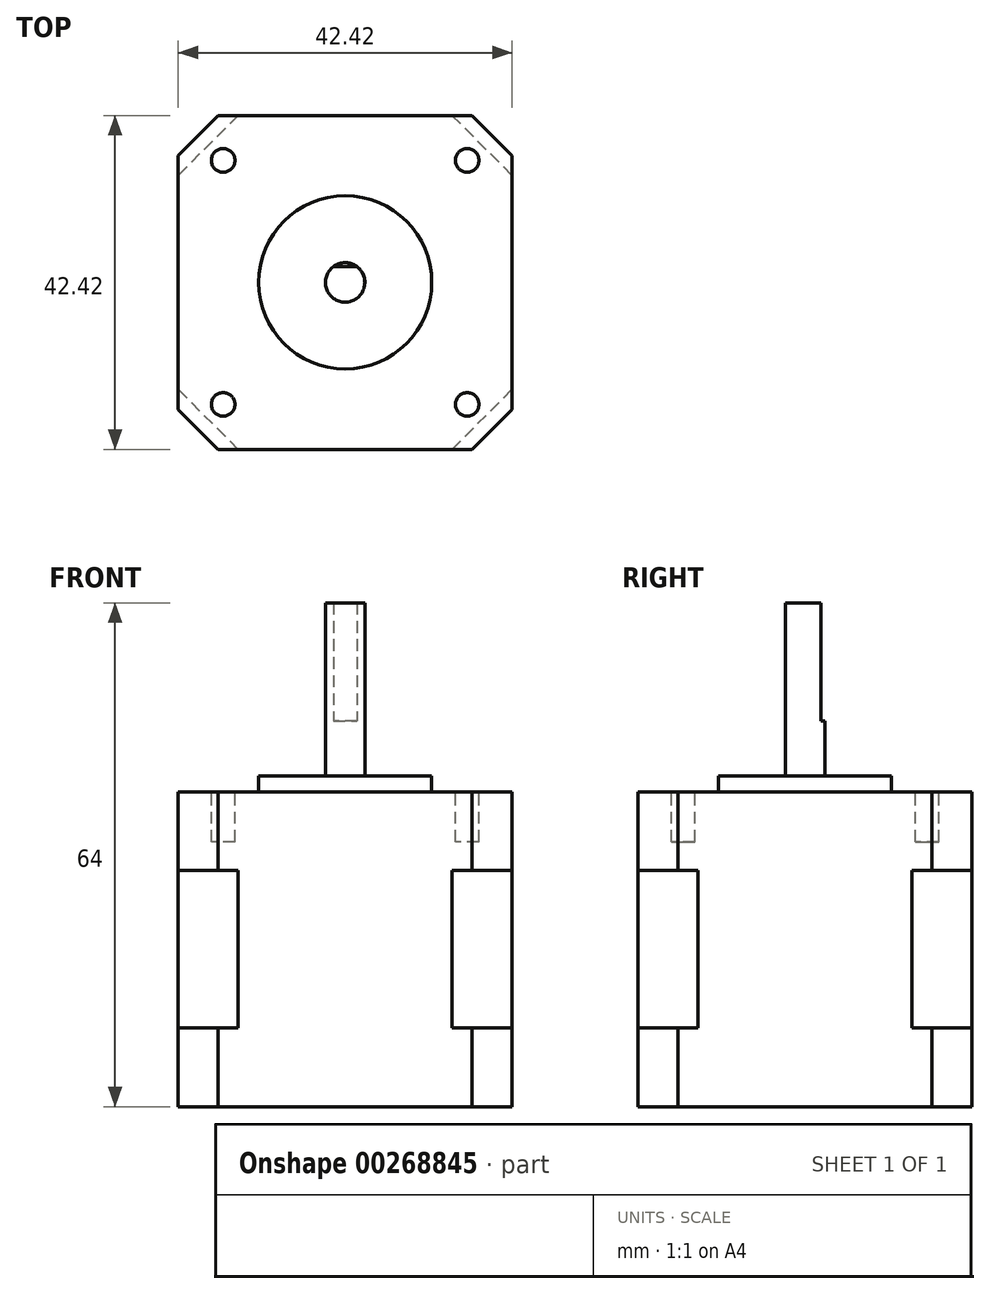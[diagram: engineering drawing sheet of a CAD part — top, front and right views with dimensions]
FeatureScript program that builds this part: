
annotation { "Feature Type Name" : "Feature", "Feature Type Description" : "" }
export const myFeature = defineFeature(function(context is Context, id is Id, definition is map)
    precondition{}
    {
        {
            var Q0;
            Q0=qCreatedBy(makeId("Top.planeOp"),FACE);
            var sketch = newSketch(context, id + "F0", { "sketchPlane" : qUnion([Q0])});
            skLineSegment(sketch, "E0.bottom", {"start": v(-21.2, 21.2) * mm, "end": v(21.2, 21.2) * mm});
            skLineSegment(sketch, "E0.top", {"start": v(-21.2, -21.2) * mm, "end": v(21.2, -21.2) * mm});
            skLineSegment(sketch, "E0.left", {"start": v(-21.2, 21.2) * mm, "end": v(-21.2, -21.2) * mm});
            skLineSegment(sketch, "E0.right", {"start": v(21.2, 21.2) * mm, "end": v(21.2, -21.2) * mm});
            skSolve(sketch);
        }
        {
            var Q0;
            Q0=makeQuery(id+"F0.imprint","IMPRINT",FACE,{"disambiguationData":[TD([[makeQuery(id+"F0.imprint","IMPRINT",EDGE,{"derivedFrom":sQuery(id+"F0.wireOp",EDGE,"E0.bottom")}),-1.0]])]});
            extrude(context, id + "F1", {"entities" : qUnion([Q0]), "endBound" : BoundingType.SYMMETRIC, "depth" : 20 * mm});
        }
        {
            var Q0;
            Q0=makeQuery(id+"F1.opExtrude","SWEPT_EDGE",EDGE,{"disambiguationData":[OSD([sQuery(id+"F0.wireOp",EDGE,"E0.bottom"),sQuery(id+"F0.wireOp",EDGE,"E0.right")])]});
            var Q1;
            Q1=makeQuery(id+"F1.opExtrude","SWEPT_EDGE",EDGE,{"disambiguationData":[OSD([sQuery(id+"F0.wireOp",EDGE,"E0.bottom"),sQuery(id+"F0.wireOp",EDGE,"E0.left")])]});
            var Q2;
            Q2=makeQuery(id+"F1.opExtrude","SWEPT_EDGE",EDGE,{"disambiguationData":[OSD([sQuery(id+"F0.wireOp",EDGE,"E0.top"),sQuery(id+"F0.wireOp",EDGE,"E0.left")])]});
            var Q3;
            Q3=makeQuery(id+"F1.opExtrude","SWEPT_EDGE",EDGE,{"disambiguationData":[OSD([sQuery(id+"F0.wireOp",EDGE,"E0.top"),sQuery(id+"F0.wireOp",EDGE,"E0.right")])]});
            chamfer(context, id + "F2", {"entities" : qUnion([Q0, Q1, Q2, Q3]), "width" : 7.62 * mm, "tangentPropagation" : true});
        }
        {
            var Q0;
            Q0=makeQuery(id+"F1.opExtrude","CAP_FACE",FACE,{"disambiguationData":[OSD([sQuery(id+"F0.wireOp",EDGE,"E0.bottom"),sQuery(id+"F0.wireOp",EDGE,"E0.top"),sQuery(id+"F0.wireOp",EDGE,"E0.left"),sQuery(id+"F0.wireOp",EDGE,"E0.right")])],"isStart":false});
            var sketch = newSketch(context, id + "F3", { "sketchPlane" : qUnion([Q0])});
            skLineSegment(sketch, "E1.bottom", {"start": v(-21.2, 21.2) * mm, "end": v(21.2, 21.2) * mm});
            skLineSegment(sketch, "E1.top", {"start": v(-21.2, -21.2) * mm, "end": v(21.2, -21.2) * mm});
            skLineSegment(sketch, "E1.left", {"start": v(-21.2, 21.2) * mm, "end": v(-21.2, -21.2) * mm});
            skLineSegment(sketch, "E1.right", {"start": v(21.2, 21.2) * mm, "end": v(21.2, -21.2) * mm});
            skSolve(sketch);
        }
        {
            var Q0;
            {var subQ0=sQuery(id+"F0.wireOp",EDGE,"E0.top");var subQ1=sQuery(id+"F0.wireOp",EDGE,"E0.right");var subQ2=sQuery(id+"F0.wireOp",EDGE,"E0.bottom");var subQ3=sQuery(id+"F0.wireOp",EDGE,"E0.left");var subQ4=makeQuery(id+"F1.opExtrude","CAP_FACE",FACE,{"disambiguationData":[OSD([subQ2,subQ0,subQ3,subQ1])],"isStart":false});var subQ8=makeQuery(id+"F2.opChamfer","BLEND_EDGE",EDGE,{"blendedFrom":[makeQuery(id+"F1.opExtrude","SWEPT_EDGE",EDGE,{"disambiguationData":[OSD([subQ2,subQ3])]}),subQ4],"blendedInto":[subQ4]});Q0=makeQuery(id+"F3.imprint","IMPRINT",FACE,{"disambiguationData":[TD([[makeQuery(id+"F3.imprint","IMPRINT",EDGE,{"derivedFrom":subQ8}),1.0]])]});}
            var Q1;
            {var subQ0=sQuery(id+"F0.wireOp",EDGE,"E0.bottom");var subQ1=sQuery(id+"F0.wireOp",EDGE,"E0.right");var subQ2=makeQuery(id+"F2.opChamfer","BLEND_EDGE",EDGE,{"blendedFrom":[makeQuery(id+"F1.opExtrude","SWEPT_EDGE",EDGE,{"disambiguationData":[OSD([subQ0,subQ1])]}),makeQuery(id+"F1.opExtrude","CAP_FACE",FACE,{"disambiguationData":[OSD([subQ0,sQuery(id+"F0.wireOp",EDGE,"E0.top"),sQuery(id+"F0.wireOp",EDGE,"E0.left"),subQ1])],"isStart":false})],"blendedInto":[makeQuery(id+"F1.opExtrude","CAP_FACE",FACE,{"disambiguationData":[OSD([subQ0,sQuery(id+"F0.wireOp",EDGE,"E0.top"),sQuery(id+"F0.wireOp",EDGE,"E0.left"),subQ1])],"isStart":false})]});Q1=makeQuery(id+"F3.imprint","IMPRINT",FACE,{"disambiguationData":[TD([[makeQuery(id+"F3.imprint","IMPRINT",EDGE,{"derivedFrom":subQ2}),-1.0]])]});}
            var Q2;
            {var subQ0=sQuery(id+"F0.wireOp",EDGE,"E0.bottom");var subQ1=sQuery(id+"F0.wireOp",EDGE,"E0.left");var subQ2=makeQuery(id+"F2.opChamfer","BLEND_EDGE",EDGE,{"blendedFrom":[makeQuery(id+"F1.opExtrude","SWEPT_EDGE",EDGE,{"disambiguationData":[OSD([subQ0,subQ1])]}),makeQuery(id+"F1.opExtrude","CAP_FACE",FACE,{"disambiguationData":[OSD([subQ0,sQuery(id+"F0.wireOp",EDGE,"E0.top"),subQ1,sQuery(id+"F0.wireOp",EDGE,"E0.right")])],"isStart":false})],"blendedInto":[makeQuery(id+"F1.opExtrude","CAP_FACE",FACE,{"disambiguationData":[OSD([subQ0,sQuery(id+"F0.wireOp",EDGE,"E0.top"),subQ1,sQuery(id+"F0.wireOp",EDGE,"E0.right")])],"isStart":false})]});Q2=makeQuery(id+"F3.imprint","IMPRINT",FACE,{"disambiguationData":[TD([[makeQuery(id+"F3.imprint","IMPRINT",EDGE,{"derivedFrom":subQ2}),-1.0]])]});}
            var Q3;
            {var subQ0=sQuery(id+"F0.wireOp",EDGE,"E0.top");var subQ1=sQuery(id+"F0.wireOp",EDGE,"E0.left");var subQ2=makeQuery(id+"F2.opChamfer","BLEND_EDGE",EDGE,{"blendedFrom":[makeQuery(id+"F1.opExtrude","SWEPT_EDGE",EDGE,{"disambiguationData":[OSD([subQ0,subQ1])]}),makeQuery(id+"F1.opExtrude","CAP_FACE",FACE,{"disambiguationData":[OSD([sQuery(id+"F0.wireOp",EDGE,"E0.bottom"),subQ0,subQ1,sQuery(id+"F0.wireOp",EDGE,"E0.right")])],"isStart":false})],"blendedInto":[makeQuery(id+"F1.opExtrude","CAP_FACE",FACE,{"disambiguationData":[OSD([sQuery(id+"F0.wireOp",EDGE,"E0.bottom"),subQ0,subQ1,sQuery(id+"F0.wireOp",EDGE,"E0.right")])],"isStart":false})]});Q3=makeQuery(id+"F3.imprint","IMPRINT",FACE,{"disambiguationData":[TD([[makeQuery(id+"F3.imprint","IMPRINT",EDGE,{"derivedFrom":subQ2}),-1.0]])]});}
            var Q4;
            {var subQ0=sQuery(id+"F0.wireOp",EDGE,"E0.top");var subQ1=sQuery(id+"F0.wireOp",EDGE,"E0.right");var subQ2=makeQuery(id+"F2.opChamfer","BLEND_EDGE",EDGE,{"blendedFrom":[makeQuery(id+"F1.opExtrude","SWEPT_EDGE",EDGE,{"disambiguationData":[OSD([subQ0,subQ1])]}),makeQuery(id+"F1.opExtrude","CAP_FACE",FACE,{"disambiguationData":[OSD([sQuery(id+"F0.wireOp",EDGE,"E0.bottom"),subQ0,sQuery(id+"F0.wireOp",EDGE,"E0.left"),subQ1])],"isStart":false})],"blendedInto":[makeQuery(id+"F1.opExtrude","CAP_FACE",FACE,{"disambiguationData":[OSD([sQuery(id+"F0.wireOp",EDGE,"E0.bottom"),subQ0,sQuery(id+"F0.wireOp",EDGE,"E0.left"),subQ1])],"isStart":false})]});Q4=makeQuery(id+"F3.imprint","IMPRINT",FACE,{"disambiguationData":[TD([[makeQuery(id+"F3.imprint","IMPRINT",EDGE,{"derivedFrom":subQ2}),-1.0]])]});}
            extrude(context, id + "F4", {"entities" : qUnion([Q0, Q1, Q2, Q3, Q4]), "operationType" : NewBodyOperationType.ADD, "depth" : 10 * mm});
        }
        {
            var Q0;
            Q0=makeQuery(id+"F4.opExtrude","SWEPT_EDGE",EDGE,{"disambiguationData":[OSD([sQuery(id+"F3.wireOp",EDGE,"E1.bottom"),sQuery(id+"F3.wireOp",EDGE,"E1.right")])]});
            var Q1;
            Q1=makeQuery(id+"F4.opExtrude","SWEPT_EDGE",EDGE,{"disambiguationData":[OSD([sQuery(id+"F3.wireOp",EDGE,"E1.bottom"),sQuery(id+"F3.wireOp",EDGE,"E1.left")])]});
            var Q2;
            Q2=makeQuery(id+"F4.opExtrude","SWEPT_EDGE",EDGE,{"disambiguationData":[OSD([sQuery(id+"F3.wireOp",EDGE,"E1.top"),sQuery(id+"F3.wireOp",EDGE,"E1.left")])]});
            var Q3;
            Q3=makeQuery(id+"F4.opExtrude","SWEPT_EDGE",EDGE,{"disambiguationData":[OSD([sQuery(id+"F3.wireOp",EDGE,"E1.top"),sQuery(id+"F3.wireOp",EDGE,"E1.right")])]});
            chamfer(context, id + "F5", {"entities" : qUnion([Q0, Q1, Q2, Q3]), "width" : 5.08 * mm, "tangentPropagation" : true});
        }
        {
            var Q0;
            Q0=makeQuery(id+"F1.opExtrude","CAP_FACE",FACE,{"disambiguationData":[OSD([sQuery(id+"F0.wireOp",EDGE,"E0.bottom"),sQuery(id+"F0.wireOp",EDGE,"E0.top"),sQuery(id+"F0.wireOp",EDGE,"E0.left"),sQuery(id+"F0.wireOp",EDGE,"E0.right")])],"isStart":true});
            var sketch = newSketch(context, id + "F6", { "sketchPlane" : qUnion([Q0])});
            skLineSegment(sketch, "E2.0.0", {"start": v(-16.13, 21.2) * mm, "end": v(16.13, 21.2) * mm});
            skLineSegment(sketch, "E2.0.1", {"start": v(16.13, 21.2) * mm, "end": v(21.2, 16.13) * mm});
            skLineSegment(sketch, "E2.0.2", {"start": v(21.2, -16.13) * mm, "end": v(21.2, 16.13) * mm});
            skLineSegment(sketch, "E2.0.3", {"start": v(21.2, -16.13) * mm, "end": v(16.13, -21.2) * mm});
            skLineSegment(sketch, "E2.0.4", {"start": v(-16.13, -21.2) * mm, "end": v(16.13, -21.2) * mm});
            skLineSegment(sketch, "E2.0.5", {"start": v(-16.13, -21.2) * mm, "end": v(-21.2, -16.13) * mm});
            skLineSegment(sketch, "E2.0.6", {"start": v(-21.2, -16.13) * mm, "end": v(-21.2, 16.13) * mm});
            skLineSegment(sketch, "E2.0.7", {"start": v(-21.2, 16.13) * mm, "end": v(-16.13, 21.2) * mm});
            skSolve(sketch);
        }
        {
            var Q0;
            {var subQ3=sQuery(id+"F6.wireOp",EDGE,"E2.0.7");Q0=makeQuery(id+"F6.imprint","IMPRINT",FACE,{"disambiguationData":[TD([[makeQuery(id+"F6.imprint","IMPRINT",EDGE,{"derivedFrom":subQ3}),-1.0]])]});}
            var Q1;
            {var subQ4=sQuery(id+"F6.wireOp",EDGE,"E2.0.1");Q1=makeQuery(id+"F6.imprint","IMPRINT",FACE,{"disambiguationData":[TD([[makeQuery(id+"F6.imprint","IMPRINT",EDGE,{"derivedFrom":subQ4}),-1.0]])]});}
            var Q2;
            {var subQ4=sQuery(id+"F6.wireOp",EDGE,"E2.0.3");Q2=makeQuery(id+"F6.imprint","IMPRINT",FACE,{"disambiguationData":[TD([[makeQuery(id+"F6.imprint","IMPRINT",EDGE,{"derivedFrom":subQ4}),-1.0]])]});}
            var Q3;
            {var subQ4=sQuery(id+"F6.wireOp",EDGE,"E2.0.5");Q3=makeQuery(id+"F6.imprint","IMPRINT",FACE,{"disambiguationData":[TD([[makeQuery(id+"F6.imprint","IMPRINT",EDGE,{"derivedFrom":subQ4}),-1.0]])]});}
            var Q4;
            {var subQ0=sQuery(id+"F0.wireOp",EDGE,"E0.top");var subQ1=sQuery(id+"F0.wireOp",EDGE,"E0.right");var subQ2=sQuery(id+"F0.wireOp",EDGE,"E0.bottom");var subQ3=sQuery(id+"F0.wireOp",EDGE,"E0.left");var subQ4=makeQuery(id+"F1.opExtrude","CAP_FACE",FACE,{"disambiguationData":[OSD([subQ2,subQ0,subQ3,subQ1])],"isStart":true});var subQ8=makeQuery(id+"F2.opChamfer","BLEND_EDGE",EDGE,{"blendedFrom":[makeQuery(id+"F1.opExtrude","SWEPT_EDGE",EDGE,{"disambiguationData":[OSD([subQ2,subQ3])]}),subQ4],"blendedInto":[subQ4]});Q4=makeQuery(id+"F6.imprint","IMPRINT",FACE,{"disambiguationData":[TD([[makeQuery(id+"F6.imprint","IMPRINT",EDGE,{"derivedFrom":subQ8}),1.0]])]});}
            extrude(context, id + "F7", {"entities" : qUnion([Q0, Q1, Q2, Q3, Q4]), "operationType" : NewBodyOperationType.ADD, "depth" : 10 * mm});
        }
        {
            var Q0;
            Q0=makeQuery(id+"F4.opExtrude","CAP_FACE",FACE,{"disambiguationData":[OSD([sQuery(id+"F3.wireOp",EDGE,"E1.bottom"),sQuery(id+"F3.wireOp",EDGE,"E1.top"),sQuery(id+"F3.wireOp",EDGE,"E1.left"),sQuery(id+"F3.wireOp",EDGE,"E1.right")])],"isStart":false});
            var sketch = newSketch(context, id + "F8", { "sketchPlane" : qUnion([Q0])});
            skCircle(sketch, "E3", {"center": v(0, 0) * mm, "radius": 11 * mm});
            skSolve(sketch);
        }
        {
            var Q0;
            Q0=makeQuery(id+"F8.imprint","IMPRINT",FACE,{"disambiguationData":[TD([[makeQuery(id+"F8.imprint","IMPRINT",EDGE,{"derivedFrom":sQuery(id+"F8.wireOp",EDGE,"E3")}),1.0]])]});
            extrude(context, id + "F9", {"entities" : qUnion([Q0]), "operationType" : NewBodyOperationType.ADD, "depth" : 2 * mm});
        }
        {
            var Q0;
            Q0=makeQuery(id+"F9.opExtrude","CAP_FACE",FACE,{"disambiguationData":[OSD([sQuery(id+"F8.wireOp",EDGE,"E3")])],"isStart":false});
            var sketch = newSketch(context, id + "F10", { "sketchPlane" : qUnion([Q0])});
            skCircle(sketch, "E4", {"center": v(0, 0) * mm, "radius": 2.5 * mm});
            skSolve(sketch);
        }
        {
            var Q0;
            Q0=makeQuery(id+"F10.imprint","IMPRINT",FACE,{"disambiguationData":[TD([[makeQuery(id+"F10.imprint","IMPRINT",EDGE,{"derivedFrom":sQuery(id+"F10.wireOp",EDGE,"E4")}),1.0]])]});
            extrude(context, id + "F11", {"entities" : qUnion([Q0]), "operationType" : NewBodyOperationType.ADD, "depth" : 22 * mm});
        }
        {
            var Q0;
            Q0=makeQuery(id+"F11.opExtrude","CAP_FACE",FACE,{"disambiguationData":[OSD([sQuery(id+"F10.wireOp",EDGE,"E4")])],"isStart":false});
            var sketch = newSketch(context, id + "F12", { "sketchPlane" : qUnion([Q0])});
            skLineSegment(sketch, "E5.bottom", {"start": v(-2.63, 2.93) * mm, "end": v(2.62, 2.93) * mm});
            skLineSegment(sketch, "E5.top", {"start": v(-2.63, 2) * mm, "end": v(2.62, 2) * mm});
            skLineSegment(sketch, "E5.left", {"start": v(-2.63, 2.93) * mm, "end": v(-2.63, 2) * mm});
            skLineSegment(sketch, "E5.right", {"start": v(2.62, 2.93) * mm, "end": v(2.62, 2) * mm});
            skSolve(sketch);
        }
        {
            var Q0;
            {var subQ0=makeQuery(id+"F11.opExtrude","CAP_EDGE",EDGE,{"disambiguationData":[OSD([sQuery(id+"F10.wireOp",EDGE,"E4")])],"isStart":false});var subQ1=sQuery(id+"F12.wireOp",EDGE,"E5.top");var subQ3=makeQuery(id+"F12.imprint","INTERSECT",VERTEX,{"disambiguationData":[OD(0.0)],"derivedFrom":[subQ0,subQ1]});Q0=qUnion([makeQuery(id+"F12.imprint","IMPRINT",FACE,{"disambiguationData":[TD([[makeQuery(id+"F12.imprint","IMPRINT",EDGE,{"derivedFrom":sQuery(id+"F12.wireOp",EDGE,"E5.bottom")}),-1.0]])]}),makeQuery(id+"F12.imprint","IMPRINT",FACE,{"disambiguationData":[TD([[makeQuery(id+"F12.imprint","IMPRINT",EDGE,{"disambiguationData":[TD([[subQ3,-1.0]])],"derivedFrom":subQ1}),1.0]])]})]);}
            extrude(context, id + "F13", {"entities" : qUnion([Q0]), "operationType" : NewBodyOperationType.REMOVE, "oppositeDirection" : true, "depth" : 15 * mm});
        }
        {
            var Q0;
            Q0=makeQuery(id+"F4.opExtrude","CAP_FACE",FACE,{"disambiguationData":[OSD([sQuery(id+"F3.wireOp",EDGE,"E1.bottom"),sQuery(id+"F3.wireOp",EDGE,"E1.top"),sQuery(id+"F3.wireOp",EDGE,"E1.left"),sQuery(id+"F3.wireOp",EDGE,"E1.right")])],"isStart":false});
            var sketch = newSketch(context, id + "F14", { "sketchPlane" : qUnion([Q0])});
            skCircle(sketch, "E6", {"center": v(-15.5, 15.5) * mm, "radius": 1.5 * mm});
            skCircle(sketch, "E7", {"center": v(15.5, 15.5) * mm, "radius": 1.5 * mm});
            skCircle(sketch, "E8", {"center": v(15.5, -15.5) * mm, "radius": 1.5 * mm});
            skCircle(sketch, "E9", {"center": v(-15.5, -15.5) * mm, "radius": 1.5 * mm});
            skLineSegment(sketch, "E10", {"start": v(-45.53, 0) * mm, "end": v(50.04, 0) * mm, "construction": true});
            skLineSegment(sketch, "E11", {"start": v(0, -35.63) * mm, "end": v(0, 35.98) * mm, "construction": true});
            skLineSegment(sketch, "E12.rect.bottom", {"start": v(-15.5, 15.5) * mm, "end": v(15.5, 15.5) * mm, "construction": true});
            skLineSegment(sketch, "E12.rect.top", {"start": v(-15.5, -15.5) * mm, "end": v(15.5, -15.5) * mm, "construction": true});
            skLineSegment(sketch, "E12.rect.left", {"start": v(-15.5, 15.5) * mm, "end": v(-15.5, -15.5) * mm, "construction": true});
            skLineSegment(sketch, "E12.rect.right", {"start": v(15.5, 15.5) * mm, "end": v(15.5, -15.5) * mm, "construction": true});
            skPoint(sketch, "E12.rect.middle", {"position": v(0, 0) * mm});
            skPoint(sketch, "E13", {"position": v(0, 15.5) * mm});
            skSolve(sketch);
        }
        {
            var Q0;
            {Q0=qUnion([makeQuery(id+"F14.imprint","IMPRINT",FACE,{"disambiguationData":[TD([[makeQuery(id+"F14.imprint","IMPRINT",EDGE,{"derivedFrom":sQuery(id+"F14.wireOp",EDGE,"E6")}),1.0]])]}),makeQuery(id+"F14.imprint","IMPRINT",FACE,{"disambiguationData":[TD([[makeQuery(id+"F14.imprint","IMPRINT",EDGE,{"derivedFrom":sQuery(id+"F14.wireOp",EDGE,"E7")}),1.0]])]}),makeQuery(id+"F14.imprint","IMPRINT",FACE,{"disambiguationData":[TD([[makeQuery(id+"F14.imprint","IMPRINT",EDGE,{"derivedFrom":sQuery(id+"F14.wireOp",EDGE,"E8")}),1.0]])]}),makeQuery(id+"F14.imprint","IMPRINT",FACE,{"disambiguationData":[TD([[makeQuery(id+"F14.imprint","IMPRINT",EDGE,{"derivedFrom":sQuery(id+"F14.wireOp",EDGE,"E9")}),1.0]])]})]);}
            extrude(context, id + "F15", {"entities" : qUnion([Q0]), "operationType" : NewBodyOperationType.REMOVE, "oppositeDirection" : true, "depth" : 6.35 * mm});
        }
        {
            var Q0;
            Q0=makeQuery(id+"F1.opExtrude","SWEPT_BODY",BODY,{"disambiguationData":[OSD([sQuery(id+"F0.wireOp",EDGE,"E0.bottom"),sQuery(id+"F0.wireOp",EDGE,"E0.top"),sQuery(id+"F0.wireOp",EDGE,"E0.left"),sQuery(id+"F0.wireOp",EDGE,"E0.right")])]});
            transform(context, id + "F16", {"entities" : qUnion([Q0]), "transformType" : TransformType.TRANSLATION_3D, "dx" : 0 * mm, "dy" : 0 * mm, "dz" : 0 * mm, "makeCopy" : true});
        }
        {
            var Q0;
            Q0=makeQuery(id+"F16.opPattern","COPY",BODY,{"derivedFrom":makeQuery(id+"F1.opExtrude","SWEPT_BODY",BODY,{"disambiguationData":[OSD([sQuery(id+"F0.wireOp",EDGE,"E0.bottom"),sQuery(id+"F0.wireOp",EDGE,"E0.top"),sQuery(id+"F0.wireOp",EDGE,"E0.left"),sQuery(id+"F0.wireOp",EDGE,"E0.right")])]}),"instanceName":"1"});
            deleteBodies(context, id + "F17", {"entities" : qUnion([Q0])});
        }
    });
